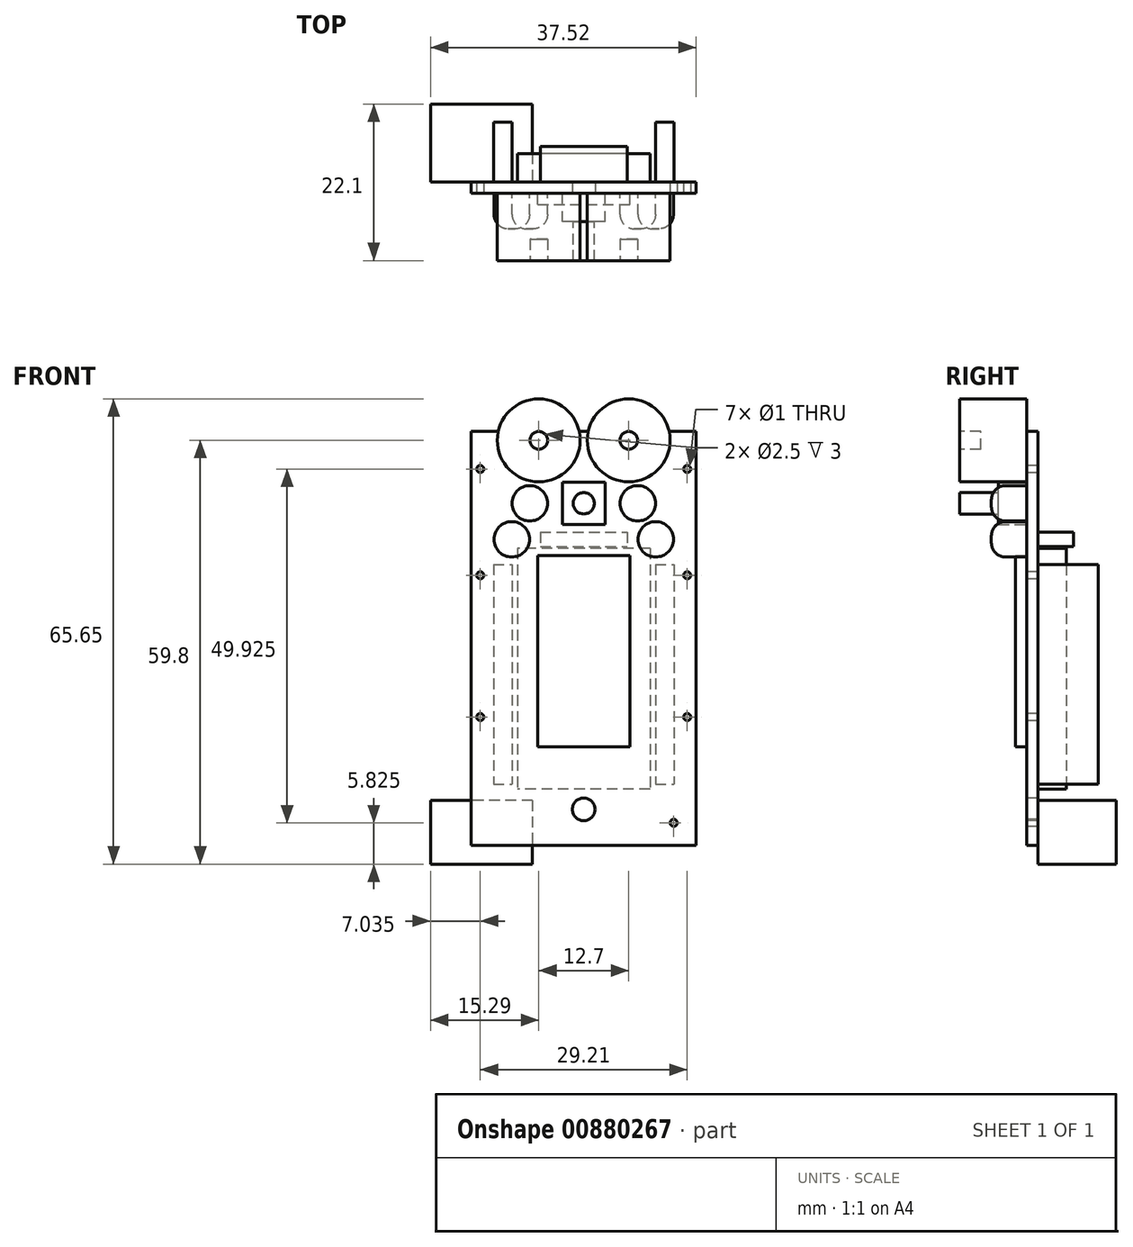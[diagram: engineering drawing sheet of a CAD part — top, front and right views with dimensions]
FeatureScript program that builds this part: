
annotation { "Feature Type Name" : "Feature", "Feature Type Description" : "" }
export const myFeature = defineFeature(function(context is Context, id is Id, definition is map)
    precondition{}
    {
        {
            var Q0;
            Q0=qCreatedBy(makeId("Front.planeOp"),FACE);
            var sketch = newSketch(context, id + "F0", { "sketchPlane" : qUnion([Q0])});
            skLineSegment(sketch, "E0.bottom", {"start": v(-15.88, 10.16) * mm, "end": v(15.88, 10.16) * mm});
            skLineSegment(sketch, "E0.top", {"start": v(-15.88, -48.26) * mm, "end": v(15.88, -48.26) * mm});
            skLineSegment(sketch, "E0.left", {"start": v(-15.88, 10.16) * mm, "end": v(-15.87, -48.26) * mm});
            skLineSegment(sketch, "E0.right", {"start": v(15.88, 10.16) * mm, "end": v(15.88, -48.26) * mm});
            skCircle(sketch, "E1", {"center": v(0, -43.18) * mm, "radius": 1.6 * mm});
            skCircle(sketch, "E2", {"center": v(-14.6, 4.84) * mm, "radius": 0.5 * mm});
            skCircle(sketch, "E3", {"center": v(-14.6, -10.16) * mm, "radius": 0.5 * mm});
            skCircle(sketch, "E4", {"center": v(-14.6, -30.16) * mm, "radius": 0.5 * mm});
            skCircle(sketch, "E5", {"center": v(14.6, 4.84) * mm, "radius": 0.5 * mm});
            skCircle(sketch, "E6", {"center": v(14.6, -10.16) * mm, "radius": 0.5 * mm});
            skCircle(sketch, "E7", {"center": v(14.6, -30.16) * mm, "radius": 0.5 * mm});
            skCircle(sketch, "E8", {"center": v(12.7, -45.08) * mm, "radius": 0.5 * mm});
            skSolve(sketch);
        }
        {
            var Q0;
            Q0=qSketchRegion(id+"F0",true);
            extrude(context, id + "F1", {"entities" : qUnion([Q0]), "oppositeDirection" : true, "depth" : 1.6 * mm, "offsetDistance" : 25.4 * mm});
        }
        {
            var Q0;
            Q0=qCreatedBy(makeId("Front.planeOp"),FACE);
            var sketch = newSketch(context, id + "F2", { "sketchPlane" : qUnion([Q0])});
            skLineSegment(sketch, "E9.bottom", {"start": v(3, -3) * mm, "end": v(-3, -3) * mm});
            skLineSegment(sketch, "E9.top", {"start": v(3, 3) * mm, "end": v(-3, 3) * mm});
            skLineSegment(sketch, "E9.left", {"start": v(3, -3) * mm, "end": v(3, 3) * mm});
            skLineSegment(sketch, "E9.right", {"start": v(-3, -3) * mm, "end": v(-3, 3) * mm});
            skPoint(sketch, "E9.middle", {"position": v(0, 0) * mm});
            skSolve(sketch);
        }
        {
            var Q0;
            Q0=qSketchRegion(id+"F2",true);
            extrude(context, id + "F3", {"entities" : qUnion([Q0]), "depth" : 4 * mm, "offsetDistance" : 25.4 * mm});
        }
        {
            var Q0;
            Q0=qCreatedBy(makeId("Front.planeOp"),FACE);
            var sketch = newSketch(context, id + "F4", { "sketchPlane" : qUnion([Q0])});
            skCircle(sketch, "E10", {"center": v(0, 0) * mm, "radius": 1.5 * mm});
            skSolve(sketch);
        }
        {
            var Q0;
            Q0=qSketchRegion(id+"F4",true);
            extrude(context, id + "F5", {"entities" : qUnion([Q0]), "operationType" : NewBodyOperationType.ADD, "depth" : 9.5 * mm, "offsetDistance" : 25.4 * mm});
        }
        {
            var Q0;
            Q0=qCreatedBy(makeId("Front.planeOp"),FACE);
            var sketch = newSketch(context, id + "F6", { "sketchPlane" : qUnion([Q0])});
            skCircle(sketch, "E11", {"center": v(-6.35, 8.89) * mm, "radius": 5.85 * mm});
            skCircle(sketch, "E12", {"center": v(6.35, 8.9) * mm, "radius": 5.85 * mm});
            skLineSegment(sketch, "E13", {"start": v(0, 15.49) * mm, "end": v(0, -15.49) * mm, "construction": true});
            skSolve(sketch);
        }
        {
            var Q0;
            Q0=qSketchRegion(id+"F6",true);
            extrude(context, id + "F7", {"entities" : qUnion([Q0]), "depth" : 9.5 * mm, "offsetDistance" : 25.4 * mm});
        }
        {
            var Q0;
            Q0=qCreatedBy(makeId("Front.planeOp"),FACE);
            var sketch = newSketch(context, id + "F8", { "sketchPlane" : qUnion([Q0])});
            skLineSegment(sketch, "E14.bottom", {"start": v(-6.5, -7.37) * mm, "end": v(6.5, -7.37) * mm});
            skLineSegment(sketch, "E14.top", {"start": v(-6.5, -34.37) * mm, "end": v(6.5, -34.37) * mm});
            skLineSegment(sketch, "E14.left", {"start": v(-6.5, -7.37) * mm, "end": v(-6.5, -34.37) * mm});
            skLineSegment(sketch, "E14.right", {"start": v(6.5, -7.37) * mm, "end": v(6.5, -34.37) * mm});
            skSolve(sketch);
        }
        {
            var Q0;
            Q0=qSketchRegion(id+"F8",true);
            extrude(context, id + "F9", {"entities" : qUnion([Q0]), "depth" : 1.6 * mm, "offsetDistance" : 25.4 * mm});
        }
        {
            var Q0;
            Q0=makeQuery(id+"F1.opExtrude","CAP_FACE",FACE,{"disambiguationData":[OSD([sQuery(id+"F0.wireOp",EDGE,"E0.bottom"),sQuery(id+"F0.wireOp",EDGE,"E0.top"),sQuery(id+"F0.wireOp",EDGE,"E0.left"),sQuery(id+"F0.wireOp",EDGE,"E0.right"),sQuery(id+"F0.wireOp",EDGE,"E1")])],"isStart":false});
            var sketch = newSketch(context, id + "F10", { "sketchPlane" : qUnion([Q0])});
            skLineSegment(sketch, "E15.bottom", {"start": v(-9.35, -6.35) * mm, "end": v(9.35, -6.35) * mm});
            skLineSegment(sketch, "E15.top", {"start": v(-9.35, -40.35) * mm, "end": v(9.35, -40.35) * mm});
            skLineSegment(sketch, "E15.left", {"start": v(-9.35, -6.35) * mm, "end": v(-9.35, -40.35) * mm});
            skLineSegment(sketch, "E15.right", {"start": v(9.35, -6.35) * mm, "end": v(9.35, -40.35) * mm});
            skSolve(sketch);
        }
        {
            var Q0;
            Q0=qSketchRegion(id+"F10",true);
            extrude(context, id + "F11", {"entities" : qUnion([Q0]), "depth" : 4 * mm, "offsetDistance" : 25.4 * mm});
        }
        {
            var Q0;
            Q0=makeQuery(id+"F1.opExtrude","CAP_FACE",FACE,{"disambiguationData":[OSD([sQuery(id+"F0.wireOp",EDGE,"E0.bottom"),sQuery(id+"F0.wireOp",EDGE,"E0.top"),sQuery(id+"F0.wireOp",EDGE,"E0.left"),sQuery(id+"F0.wireOp",EDGE,"E0.right"),sQuery(id+"F0.wireOp",EDGE,"E1")])],"isStart":false});
            var sketch = newSketch(context, id + "F12", { "sketchPlane" : qUnion([Q0])});
            skLineSegment(sketch, "E16.top", {"start": v(8.86, -39.64) * mm, "end": v(11.46, -39.64) * mm});
            skLineSegment(sketch, "E17.bottom", {"start": v(-10.13, -8.63) * mm, "end": v(-12.73, -8.63) * mm});
            skLineSegment(sketch, "E17.top", {"start": v(-10.13, -39.63) * mm, "end": v(-12.73, -39.63) * mm});
            skLineSegment(sketch, "E17.left", {"start": v(-10.13, -8.63) * mm, "end": v(-10.13, -39.63) * mm});
            skLineSegment(sketch, "E17.right", {"start": v(-12.73, -8.63) * mm, "end": v(-12.73, -39.63) * mm});
            skPoint(sketch, "E17.middle", {"position": v(-11.43, -24.13) * mm});
            skLineSegment(sketch, "E18.bottom", {"start": v(12.73, -8.63) * mm, "end": v(10.13, -8.63) * mm});
            skLineSegment(sketch, "E18.top", {"start": v(12.73, -39.63) * mm, "end": v(10.13, -39.63) * mm});
            skLineSegment(sketch, "E18.left", {"start": v(12.73, -8.63) * mm, "end": v(12.73, -39.63) * mm});
            skLineSegment(sketch, "E18.right", {"start": v(10.13, -8.63) * mm, "end": v(10.13, -39.63) * mm});
            skPoint(sketch, "E18.middle", {"position": v(11.43, -24.13) * mm});
            skSolve(sketch);
        }
        {
            var Q0;
            Q0=qSketchRegion(id+"F12",true);
            extrude(context, id + "F13", {"entities" : qUnion([Q0]), "depth" : 8.45 * mm, "offsetDistance" : 25.4 * mm});
        }
        {
            var Q0;
            Q0=makeQuery(id+"F1.opExtrude","CAP_FACE",FACE,{"disambiguationData":[OSD([sQuery(id+"F0.wireOp",EDGE,"E0.bottom"),sQuery(id+"F0.wireOp",EDGE,"E0.top"),sQuery(id+"F0.wireOp",EDGE,"E0.left"),sQuery(id+"F0.wireOp",EDGE,"E0.right"),sQuery(id+"F0.wireOp",EDGE,"E1")])],"isStart":false});
            var sketch = newSketch(context, id + "F14", { "sketchPlane" : qUnion([Q0])});
            skLineSegment(sketch, "E19.bottom", {"start": v(7.24, -41.9) * mm, "end": v(21.64, -41.9) * mm});
            skLineSegment(sketch, "E19.top", {"start": v(7.24, -50.9) * mm, "end": v(21.64, -50.9) * mm});
            skLineSegment(sketch, "E19.left", {"start": v(7.24, -41.9) * mm, "end": v(7.24, -50.9) * mm});
            skLineSegment(sketch, "E19.right", {"start": v(21.64, -41.9) * mm, "end": v(21.64, -50.9) * mm});
            skSolve(sketch);
        }
        {
            var Q0;
            Q0=qSketchRegion(id+"F14",true);
            extrude(context, id + "F15", {"entities" : qUnion([Q0]), "depth" : 11 * mm, "offsetDistance" : 25.4 * mm});
        }
        {
            var Q0;
            Q0=makeQuery(id+"F1.opExtrude","CAP_FACE",FACE,{"disambiguationData":[OSD([sQuery(id+"F0.wireOp",EDGE,"E0.bottom"),sQuery(id+"F0.wireOp",EDGE,"E0.top"),sQuery(id+"F0.wireOp",EDGE,"E0.left"),sQuery(id+"F0.wireOp",EDGE,"E0.right"),sQuery(id+"F0.wireOp",EDGE,"E1")])],"isStart":false});
            var sketch = newSketch(context, id + "F16", { "sketchPlane" : qUnion([Q0])});
            skLineSegment(sketch, "E20.bottom", {"start": v(6.15, -4.08) * mm, "end": v(-6.15, -4.08) * mm});
            skLineSegment(sketch, "E20.top", {"start": v(6.15, -6.08) * mm, "end": v(-6.15, -6.08) * mm});
            skLineSegment(sketch, "E20.left", {"start": v(6.15, -4.08) * mm, "end": v(6.15, -6.08) * mm});
            skLineSegment(sketch, "E20.right", {"start": v(-6.15, -4.08) * mm, "end": v(-6.15, -6.08) * mm});
            skPoint(sketch, "E20.middle", {"position": v(0, -5.08) * mm});
            skSolve(sketch);
        }
        {
            var Q0;
            Q0=qSketchRegion(id+"F16",true);
            extrude(context, id + "F17", {"entities" : qUnion([Q0]), "depth" : 5 * mm, "offsetDistance" : 25.4 * mm});
        }
        {
            var Q0;
            Q0=qCreatedBy(makeId("Front.planeOp"),FACE);
            var sketch = newSketch(context, id + "F18", { "sketchPlane" : qUnion([Q0])});
            skCircle(sketch, "E21", {"center": v(-7.62, 0) * mm, "radius": 2.5 * mm});
            skCircle(sketch, "E22", {"center": v(7.62, 0) * mm, "radius": 2.5 * mm});
            skCircle(sketch, "E23", {"center": v(10.16, -5.08) * mm, "radius": 2.5 * mm});
            skCircle(sketch, "E24", {"center": v(-10.16, -5.08) * mm, "radius": 2.5 * mm});
            skSolve(sketch);
        }
        {
            var Q0;
            Q0=qSketchRegion(id+"F18",true);
            extrude(context, id + "F19", {"entities" : qUnion([Q0]), "depth" : 5 * mm, "offsetDistance" : 25.4 * mm});
        }
        {
            var Q0;
            Q0=makeQuery(id+"F19.opExtrude","CAP_FACE",FACE,{"disambiguationData":[OSD([sQuery(id+"F18.wireOp",EDGE,"E24")])],"isStart":false});
            var Q1;
            Q1=makeQuery(id+"F19.opExtrude","CAP_FACE",FACE,{"disambiguationData":[OSD([sQuery(id+"F18.wireOp",EDGE,"E21")])],"isStart":false});
            var Q2;
            Q2=makeQuery(id+"F19.opExtrude","CAP_FACE",FACE,{"disambiguationData":[OSD([sQuery(id+"F18.wireOp",EDGE,"E22")])],"isStart":false});
            var Q3;
            Q3=makeQuery(id+"F19.opExtrude","CAP_FACE",FACE,{"disambiguationData":[OSD([sQuery(id+"F18.wireOp",EDGE,"E23")])],"isStart":false});
            fillet(context, id + "F20", {"entities" : qUnion([Q0, Q1, Q2, Q3]), "radius" : 2 * mm, "tangentPropagation" : true, "allowEdgeOverflow" : false});
        }
        {
            var Q0;
            Q0=makeQuery(id+"F7.opExtrude","CAP_FACE",FACE,{"disambiguationData":[OSD([sQuery(id+"F6.wireOp",EDGE,"E11")])],"isStart":false});
            var sketch = newSketch(context, id + "F21", { "sketchPlane" : qUnion([Q0])});
            skCircle(sketch, "E25", {"center": v(-6.35, 8.89) * mm, "radius": 1.25 * mm});
            skCircle(sketch, "E26", {"center": v(6.35, 8.9) * mm, "radius": 1.25 * mm});
            skSolve(sketch);
        }
        {
            var Q0;
            Q0=qSketchRegion(id+"F21",true);
            extrude(context, id + "F22", {"entities" : qUnion([Q0]), "operationType" : NewBodyOperationType.REMOVE, "oppositeDirection" : true, "depth" : 3 * mm, "offsetDistance" : 25.4 * mm});
        }
    });
